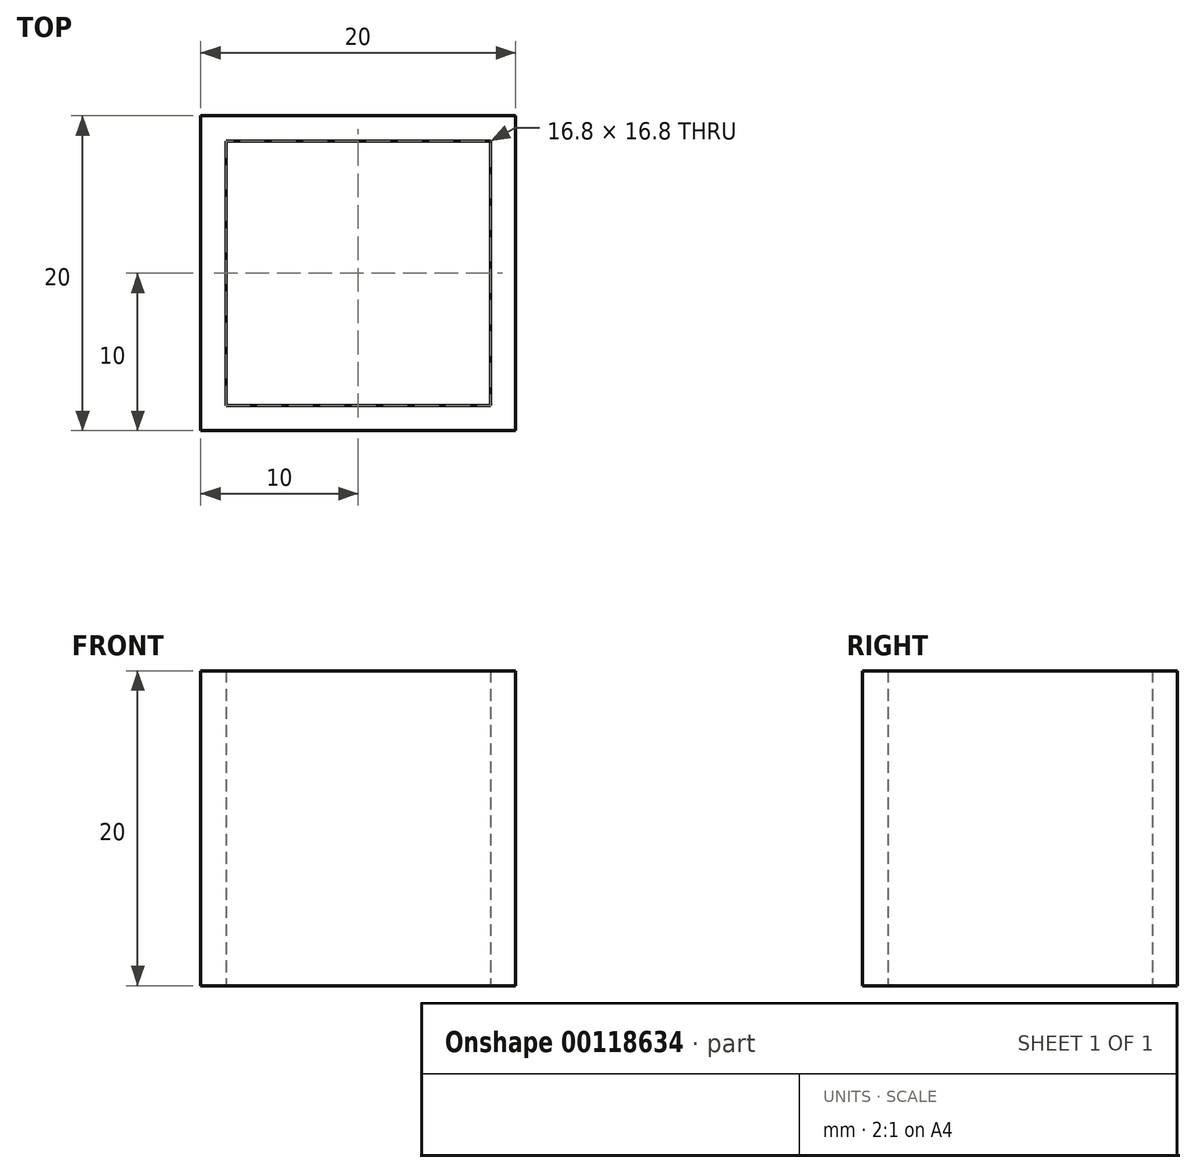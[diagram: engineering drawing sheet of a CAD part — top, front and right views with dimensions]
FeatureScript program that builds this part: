
annotation { "Feature Type Name" : "Feature", "Feature Type Description" : "" }
export const myFeature = defineFeature(function(context is Context, id is Id, definition is map)
    precondition{}
    {
        {
            var Q0;
            Q0=qCreatedBy(makeId("Top.planeOp"),FACE);
            var sketch = newSketch(context, id + "F0", { "sketchPlane" : qUnion([Q0])});
            skLineSegment(sketch, "E0.bottom", {"start": v(10, -10) * mm, "end": v(-10, -10) * mm});
            skLineSegment(sketch, "E0.top", {"start": v(10, 10) * mm, "end": v(-10, 10) * mm});
            skLineSegment(sketch, "E0.left", {"start": v(10, -10) * mm, "end": v(10, 10) * mm});
            skLineSegment(sketch, "E0.right", {"start": v(-10, -10) * mm, "end": v(-10, 10) * mm});
            skPoint(sketch, "E0.middle", {"position": v(0, 0) * mm});
            skSolve(sketch);
        }
        {
            var Q0;
            Q0=qSketchRegion(id+"F0",true);
            extrude(context, id + "F1", {"entities" : qUnion([Q0]), "depth" : 20 * mm});
        }
        {
            var Q0;
            Q0=makeQuery(id+"F1.opExtrude","CAP_FACE",FACE,{"disambiguationData":[OSD([sQuery(id+"F0.wireOp",EDGE,"E0.bottom"),sQuery(id+"F0.wireOp",EDGE,"E0.top"),sQuery(id+"F0.wireOp",EDGE,"E0.left"),sQuery(id+"F0.wireOp",EDGE,"E0.right")])],"isStart":false});
            var Q1;
            Q1=makeQuery(id+"F1.opExtrude","CAP_FACE",FACE,{"disambiguationData":[OSD([sQuery(id+"F0.wireOp",EDGE,"E0.bottom"),sQuery(id+"F0.wireOp",EDGE,"E0.top"),sQuery(id+"F0.wireOp",EDGE,"E0.left"),sQuery(id+"F0.wireOp",EDGE,"E0.right")])],"isStart":true});
            shell(context, id + "F2", {"entities" : qUnion([Q0, Q1]), "thickness" : 1.6 * mm});
        }
    });
